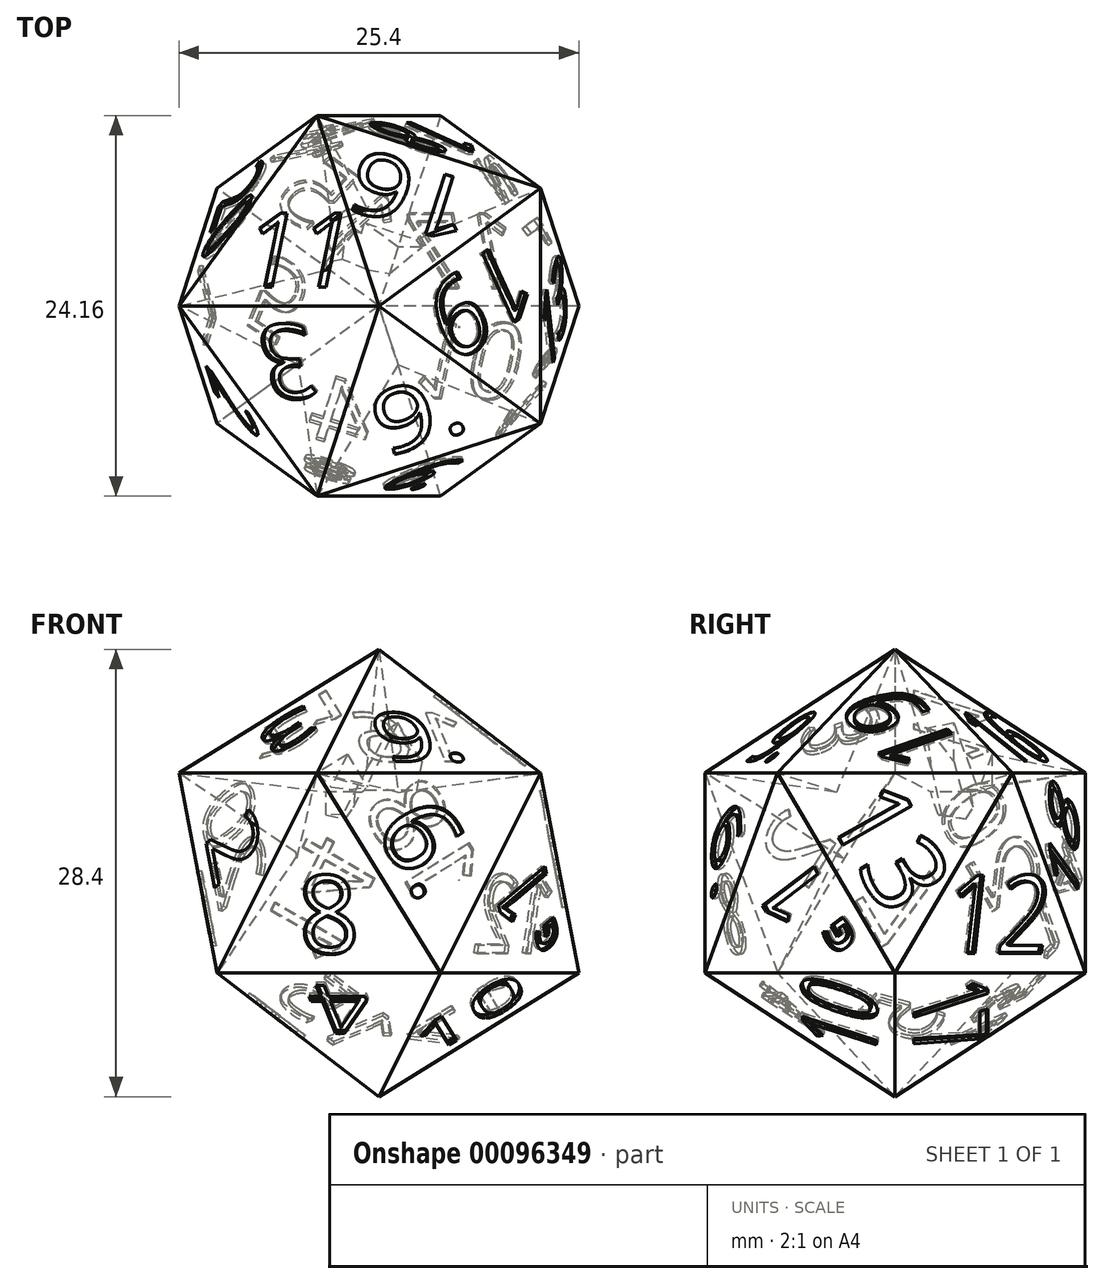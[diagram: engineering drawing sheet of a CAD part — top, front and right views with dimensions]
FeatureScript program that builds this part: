
annotation { "Feature Type Name" : "Feature", "Feature Type Description" : "" }
export const myFeature = defineFeature(function(context is Context, id is Id, definition is map)
    precondition{}
    {
        {
            var Q0;
            Q0=qCreatedBy(makeId("Top.planeOp"),FACE);
            var sketch = newSketch(context, id + "F0", { "sketchPlane" : qUnion([Q0])});
            skCircle(sketch, "E0.cCircle", {"center": v(0, 0) * mm, "radius": 12.7 * mm, "construction": true});
            skLineSegment(sketch, "E0.0", {"start": v(10.27, 7.46) * mm, "end": v(10.27, -7.46) * mm});
            skLineSegment(sketch, "E0.1", {"start": v(10.27, -7.46) * mm, "end": v(-3.92, -12.08) * mm});
            skLineSegment(sketch, "E0.2", {"start": v(-3.92, -12.08) * mm, "end": v(-12.7, 0) * mm});
            skLineSegment(sketch, "E0.3", {"start": v(-12.7, 0) * mm, "end": v(-3.92, 12.08) * mm});
            skLineSegment(sketch, "E0.4", {"start": v(-3.92, 12.08) * mm, "end": v(10.27, 7.46) * mm});
            skLineSegment(sketch, "E1", {"start": v(0, 0) * mm, "end": v(-3.92, -12.08) * mm, "construction": true});
            skSolve(sketch);
        }
        {
            var Q0;
            Q0=qCreatedBy(makeId("Right.planeOp"),FACE);
            var sketch = newSketch(context, id + "F1", { "sketchPlane" : qUnion([Q0])});
            skLineSegment(sketch, "E2", {"start": v(0, 0) * mm, "end": v(0, 7.85) * mm, "construction": true});
            skSolve(sketch);
        }
        {
            var Q0;
            Q0=sQuery(id+"F0.wireOp",VERTEX,"E0.1.start");
            var Q1;
            Q1=sQuery(id+"F0.wireOp",VERTEX,"E0.2.start");
            var Q2;
            Q2=sQuery(id+"F1.wireOp",VERTEX,"E2.end");
            cPlane(context, id + "F2", {"entities" : qUnion([Q0, Q1, Q2]), "cplaneType" : CPlaneType.THREE_POINT, "offset" : 152.4 * mm, "width" : 152.4 * mm, "height" : 152.4 * mm});
        }
        {
            var Q0;
            Q0=qCreatedBy(id+"F2.planeOp",FACE);
            var sketch = newSketch(context, id + "F3", { "sketchPlane" : qUnion([Q0])});
            skPoint(sketch, "E3.0", {"position": v(-5.19, -9.77) * mm});
            skPoint(sketch, "E4.0", {"position": v(9.27, -6.04) * mm});
            skPoint(sketch, "E5.0", {"position": v(-1.2, 4.61) * mm});
            skLineSegment(sketch, "E6", {"start": v(-5.19, -9.77) * mm, "end": v(-1.2, 4.61) * mm});
            skLineSegment(sketch, "E7", {"start": v(9.27, -6.04) * mm, "end": v(-1.2, 4.61) * mm});
            skLineSegment(sketch, "E8", {"start": v(9.27, -6.04) * mm, "end": v(-5.19, -9.77) * mm});
            skLineSegment(sketch, "E9", {"start": v(-3.19, -2.58) * mm, "end": v(9.27, -6.04) * mm, "construction": true});
            skSolve(sketch);
        }
        {
            var Q0;
            Q0=sQuery(id+"F3.wireOp",VERTEX,"E3.0");
            var Q1;
            Q1=sQuery(id+"F0.wireOp",VERTEX,"E0.2.end");
            var Q2;
            Q2=sQuery(id+"F1.wireOp",VERTEX,"E2.end");
            cPlane(context, id + "F4", {"entities" : qUnion([Q0, Q1, Q2]), "cplaneType" : CPlaneType.THREE_POINT, "offset" : 152.4 * mm, "width" : 152.4 * mm, "height" : 152.4 * mm});
        }
        {
            var Q0;
            Q0=qCreatedBy(id+"F4.planeOp",FACE);
            var sketch = newSketch(context, id + "F5", { "sketchPlane" : qUnion([Q0])});
            skPoint(sketch, "E10.0", {"position": v(-11.06, 0) * mm});
            skPoint(sketch, "E11.0", {"position": v(-0.99, -11.02) * mm});
            skPoint(sketch, "E12.0", {"position": v(3.52, 3.21) * mm});
            skLineSegment(sketch, "E13", {"start": v(-11.06, 0) * mm, "end": v(3.52, 3.21) * mm});
            skLineSegment(sketch, "E14", {"start": v(-0.99, -11.02) * mm, "end": v(-11.06, 0) * mm});
            skLineSegment(sketch, "E15", {"start": v(-0.99, -11.02) * mm, "end": v(3.52, 3.21) * mm});
            skLineSegment(sketch, "E16", {"start": v(-11.06, 0) * mm, "end": v(1.26, -3.9) * mm, "construction": true});
            skLineSegment(sketch, "E17", {"start": v(3.52, 3.21) * mm, "end": v(-6.03, -5.5) * mm, "construction": true});
            skSolve(sketch);
        }
        {
            var Q0;
            Q0=sQuery(id+"F5.wireOp",VERTEX,"E10.0");
            var Q1;
            Q1=sQuery(id+"F0.wireOp",VERTEX,"E0.3.end");
            var Q2;
            Q2=sQuery(id+"F3.wireOp",VERTEX,"E5.0");
            cPlane(context, id + "F6", {"entities" : qUnion([Q0, Q1, Q2]), "cplaneType" : CPlaneType.THREE_POINT, "offset" : 152.4 * mm, "width" : 152.4 * mm, "height" : 152.4 * mm});
        }
        {
            var Q0;
            Q0=qCreatedBy(id+"F6.planeOp",FACE);
            var sketch = newSketch(context, id + "F7", { "sketchPlane" : qUnion([Q0])});
            skPoint(sketch, "E18.0", {"position": v(-0.99, 11.02) * mm});
            skPoint(sketch, "E19.0", {"position": v(-11.06, 0) * mm});
            skPoint(sketch, "E20.0", {"position": v(3.52, -3.21) * mm});
            skLineSegment(sketch, "E21", {"start": v(-0.99, 11.02) * mm, "end": v(3.52, -3.21) * mm});
            skLineSegment(sketch, "E22", {"start": v(3.52, -3.21) * mm, "end": v(-11.06, 0) * mm});
            skLineSegment(sketch, "E23", {"start": v(-0.99, 11.02) * mm, "end": v(-11.06, 0) * mm});
            skLineSegment(sketch, "E24", {"start": v(-6.03, 5.5) * mm, "end": v(3.52, -3.21) * mm, "construction": true});
            skSolve(sketch);
        }
        {
            var Q0;
            Q0=sQuery(id+"F0.wireOp",VERTEX,"E0.4.end");
            var Q1;
            Q1=sQuery(id+"F3.wireOp",VERTEX,"E5.0");
            var Q2;
            Q2=sQuery(id+"F0.wireOp",VERTEX,"E0.3.end");
            cPlane(context, id + "F8", {"entities" : qUnion([Q0, Q1, Q2]), "cplaneType" : CPlaneType.THREE_POINT, "offset" : 152.4 * mm, "width" : 152.4 * mm, "height" : 152.4 * mm});
        }
        {
            var Q0;
            Q0=qCreatedBy(id+"F8.planeOp",FACE);
            var sketch = newSketch(context, id + "F9", { "sketchPlane" : qUnion([Q0])});
            skPoint(sketch, "E25.0", {"position": v(-5.19, 9.77) * mm});
            skPoint(sketch, "E26.0", {"position": v(9.27, 6.04) * mm});
            skPoint(sketch, "E27.0", {"position": v(-1.2, -4.61) * mm});
            skLineSegment(sketch, "E28", {"start": v(9.27, 6.04) * mm, "end": v(-1.2, -4.61) * mm});
            skLineSegment(sketch, "E29", {"start": v(-1.2, -4.61) * mm, "end": v(-5.19, 9.77) * mm});
            skLineSegment(sketch, "E30", {"start": v(-5.19, 9.77) * mm, "end": v(9.27, 6.04) * mm});
            skSolve(sketch);
        }
        {
            var Q0;
            Q0=sQuery(id+"F0.wireOp",VERTEX,"E0.4.end");
            var Q1;
            Q1=sQuery(id+"F3.wireOp",VERTEX,"E5.0");
            var Q2;
            Q2=sQuery(id+"F3.wireOp",VERTEX,"E4.0");
            cPlane(context, id + "F10", {"entities" : qUnion([Q0, Q1, Q2]), "cplaneType" : CPlaneType.THREE_POINT, "offset" : 152.4 * mm, "width" : 152.4 * mm, "height" : 152.4 * mm});
        }
        {
            var Q0;
            Q0=qCreatedBy(id+"F10.planeOp",FACE);
            var sketch = newSketch(context, id + "F11", { "sketchPlane" : qUnion([Q0])});
            skPoint(sketch, "E31.0", {"position": v(8.16, 7.46) * mm});
            skPoint(sketch, "E32.0", {"position": v(-4.76, 0) * mm});
            skPoint(sketch, "E33.0", {"position": v(8.16, -7.46) * mm});
            skLineSegment(sketch, "E34", {"start": v(8.16, 7.46) * mm, "end": v(8.16, -7.46) * mm});
            skLineSegment(sketch, "E35", {"start": v(8.16, -7.46) * mm, "end": v(-4.76, 0) * mm});
            skLineSegment(sketch, "E36", {"start": v(8.16, 7.46) * mm, "end": v(-4.76, 0) * mm});
            skSolve(sketch);
        }
        {
            var Q0;
            Q0=sQuery(id+"F5.wireOp",EDGE,"E14");
            cPlane(context, id + "F12", {"entities" : qUnion([Q0]), "cplaneType" : CPlaneType.LINE_ANGLE, "offset" : 152.4 * mm, "angle" : 100.81 * degree, "width" : 152.4 * mm, "height" : 152.4 * mm});
        }
        {
            var Q0;
            Q0=qCreatedBy(id+"F12.planeOp",FACE);
            var sketch = newSketch(context, id + "F13", { "sketchPlane" : qUnion([Q0])});
            skLineSegment(sketch, "E37", {"start": v(7.14, -2.92) * mm, "end": v(-7.66, -0.9) * mm});
            skPoint(sketch, "E38.orphan", {"position": v(-2, -14.73) * mm});
            skPoint(sketch, "E39.start.orphan", {"position": v(-0.26, -1.91) * mm});
            skPoint(sketch, "E40.start.orphan", {"position": v(2.56, -8.82) * mm});
            skLineSegment(sketch, "E41", {"start": v(7.14, -2.92) * mm, "end": v(-2, -14.72) * mm});
            skLineSegment(sketch, "E42", {"start": v(-7.66, -0.9) * mm, "end": v(-2, -14.72) * mm});
            skLineSegment(sketch, "E43", {"start": v(-0.26, -1.91) * mm, "end": v(-2, -14.72) * mm, "construction": true});
            skLineSegment(sketch, "E44", {"start": v(-4.83, -7.81) * mm, "end": v(7.14, -2.92) * mm, "construction": true});
            skSolve(sketch);
        }
        {
            var Q0;
            Q0=makeQuery(id+"F7.imprint","IMPRINT",FACE,{"disambiguationData":[TD([[makeQuery(id+"F7.imprint","IMPRINT",EDGE,{"derivedFrom":sQuery(id+"F7.wireOp",EDGE,"E21")}),-1.0]])]});
            extrude(context, id + "F14", {"entities" : qUnion([Q0]), "oppositeDirection" : true, "depth" : 2 / 76.2 * mm});
        }
        {
            var Q0;
            Q0=makeQuery(id+"F9.imprint","IMPRINT",FACE,{"disambiguationData":[TD([[makeQuery(id+"F9.imprint","IMPRINT",EDGE,{"derivedFrom":sQuery(id+"F9.wireOp",EDGE,"E28")}),-1.0]])]});
            extrude(context, id + "F15", {"entities" : qUnion([Q0]), "operationType" : NewBodyOperationType.ADD, "oppositeDirection" : true, "depth" : 2 / 76.2 * mm});
        }
        {
            var Q0;
            Q0=makeQuery(id+"F11.imprint","IMPRINT",FACE,{"disambiguationData":[TD([[makeQuery(id+"F11.imprint","IMPRINT",EDGE,{"derivedFrom":sQuery(id+"F11.wireOp",EDGE,"E34")}),-1.0]])]});
            extrude(context, id + "F16", {"entities" : qUnion([Q0]), "operationType" : NewBodyOperationType.ADD, "depth" : 16.93 * mm});
        }
        {
            var Q0;
            Q0=makeQuery(id+"F3.imprint","IMPRINT",FACE,{"disambiguationData":[TD([[makeQuery(id+"F3.imprint","IMPRINT",EDGE,{"derivedFrom":sQuery(id+"F3.wireOp",EDGE,"E6")}),-1.0]])]});
            extrude(context, id + "F17", {"entities" : qUnion([Q0]), "operationType" : NewBodyOperationType.ADD, "oppositeDirection" : true, "depth" : 2 / 76.2 * mm});
        }
        {
            var Q0;
            Q0=makeQuery(id+"F5.imprint","IMPRINT",FACE,{"disambiguationData":[TD([[makeQuery(id+"F5.imprint","IMPRINT",EDGE,{"derivedFrom":sQuery(id+"F5.wireOp",EDGE,"E13")}),-1.0]])]});
            extrude(context, id + "F18", {"entities" : qUnion([Q0]), "operationType" : NewBodyOperationType.ADD, "oppositeDirection" : true, "depth" : 18.55 * mm});
        }
        {
            var Q0;
            Q0=qSketchRegion(id+"F13",true);
            extrude(context, id + "F19", {"entities" : qUnion([Q0]), "operationType" : NewBodyOperationType.ADD, "depth" : 2 / 76.2 * mm});
        }
        {
            var Q0;
            Q0=makeQuery(id+"F19.opExtrude","CAP_EDGE",EDGE,{"disambiguationData":[OSD([sQuery(id+"F13.wireOp",EDGE,"E42")])],"isStart":true});
            cPlane(context, id + "F20", {"entities" : qUnion([Q0]), "cplaneType" : CPlaneType.LINE_ANGLE, "offset" : 152.4 * mm, "angle" : 100.81 * degree, "width" : 152.4 * mm, "height" : 152.4 * mm});
        }
        {
            var Q0;
            Q0=qCreatedBy(id+"F20.planeOp",FACE);
            var sketch = newSketch(context, id + "F21", { "sketchPlane" : qUnion([Q0])});
            skLineSegment(sketch, "E45.0", {"start": v(0.15, 2.38) * mm, "end": v(6.81, -10.98) * mm});
            skLineSegment(sketch, "E46", {"start": v(6.81, -10.98) * mm, "end": v(-8.1, -10.07) * mm});
            skLineSegment(sketch, "E47", {"start": v(-8.1, -10.07) * mm, "end": v(0.15, 2.38) * mm});
            skLineSegment(sketch, "E48", {"start": v(-8.1, -10.07) * mm, "end": v(3.48, -4.3) * mm, "construction": true});
            skSolve(sketch);
        }
        {
            var Q0;
            Q0=qSketchRegion(id+"F21",true);
            extrude(context, id + "F22", {"entities" : qUnion([Q0]), "operationType" : NewBodyOperationType.ADD, "depth" : 16.93 * mm});
        }
        {
            var Q0;
            Q0=sQuery(id+"F5.wireOp",VERTEX,"E11.0");
            var Q1;
            Q1=sQuery(id+"F3.wireOp",VERTEX,"E4.0");
            var Q2;
            Q2=makeQuery(id+"F22.opExtrude","CAP_VERTEX",VERTEX,{"disambiguationData":[OSD([sQuery(id+"F21.wireOp",EDGE,"E46"),sQuery(id+"F21.wireOp",EDGE,"E47")])],"isStart":true});
            cPlane(context, id + "F23", {"entities" : qUnion([Q0, Q1, Q2]), "cplaneType" : CPlaneType.THREE_POINT, "offset" : 152.4 * mm, "width" : 152.4 * mm, "height" : 152.4 * mm});
        }
        {
            var Q0;
            Q0=qCreatedBy(id+"F23.planeOp",FACE);
            var sketch = newSketch(context, id + "F24", { "sketchPlane" : qUnion([Q0])});
            skLineSegment(sketch, "E49.0", {"start": v(0.9, -14.83) * mm, "end": v(-7.33, -2.38) * mm});
            skLineSegment(sketch, "E50.0", {"start": v(7.57, -1.47) * mm, "end": v(-7.33, -2.38) * mm});
            skLineSegment(sketch, "E51", {"start": v(0.9, -14.83) * mm, "end": v(7.57, -1.47) * mm});
            skLineSegment(sketch, "E52", {"start": v(4.24, -8.15) * mm, "end": v(-7.33, -2.38) * mm, "construction": true});
            skSolve(sketch);
        }
        {
            var Q0;
            Q0=makeQuery(id+"F24.imprint","IMPRINT",FACE,{"disambiguationData":[TD([[makeQuery(id+"F24.imprint","IMPRINT",EDGE,{"derivedFrom":sQuery(id+"F24.wireOp",EDGE,"E49.0")}),-1.0]])]});
            extrude(context, id + "F25", {"entities" : qUnion([Q0]), "operationType" : NewBodyOperationType.ADD, "oppositeDirection" : true, "depth" : 16.93 * mm});
        }
        {
            var Q0;
            Q0=makeQuery(id+"F14.opExtrude","CAP_EDGE",EDGE,{"disambiguationData":[OSD([sQuery(id+"F7.wireOp",EDGE,"E23")])],"isStart":true});
            cPlane(context, id + "F26", {"entities" : qUnion([Q0]), "cplaneType" : CPlaneType.LINE_ANGLE, "offset" : 152.4 * mm, "angle" : 79.18 * degree, "width" : 152.4 * mm, "height" : 152.4 * mm});
        }
        {
            var Q0;
            Q0=qCreatedBy(id+"F26.planeOp",FACE);
            var sketch = newSketch(context, id + "F27", { "sketchPlane" : qUnion([Q0])});
            skLineSegment(sketch, "E53.0", {"start": v(7.66, -0.9) * mm, "end": v(-7.14, -2.92) * mm});
            skLineSegment(sketch, "E54", {"start": v(7.66, -0.9) * mm, "end": v(2, -14.72) * mm});
            skLineSegment(sketch, "E55", {"start": v(2, -14.72) * mm, "end": v(-7.14, -2.92) * mm});
            skLineSegment(sketch, "E56", {"start": v(2, -14.72) * mm, "end": v(0.26, -1.91) * mm, "construction": true});
            skLineSegment(sketch, "E57", {"start": v(4.83, -7.81) * mm, "end": v(-7.14, -2.92) * mm, "construction": true});
            skSolve(sketch);
        }
        {
            var Q0;
            Q0=qSketchRegion(id+"F27",true);
            extrude(context, id + "F28", {"entities" : qUnion([Q0]), "operationType" : NewBodyOperationType.ADD, "depth" : 6.35 * mm});
        }
        {
            var Q0;
            Q0=sQuery(id+"F7.wireOp",VERTEX,"E19.0");
            var Q1;
            Q1=makeQuery(id+"F22.boolean.opBoolean","MERGE",VERTEX,{"derivedFrom":[makeQuery(id+"F19.opExtrude","CAP_VERTEX",VERTEX,{"disambiguationData":[OSD([sQuery(id+"F13.wireOp",EDGE,"E41"),sQuery(id+"F13.wireOp",EDGE,"E42")])],"isStart":true}),makeQuery(id+"F22.opExtrude","CAP_VERTEX",VERTEX,{"disambiguationData":[OSD([sQuery(id+"F21.wireOp",EDGE,"E45.0"),sQuery(id+"F21.wireOp",EDGE,"E46")])],"isStart":true})]});
            var Q2;
            Q2=sQuery(id+"F27.wireOp",VERTEX,"E54.end");
            cPlane(context, id + "F29", {"entities" : qUnion([Q0, Q1, Q2]), "cplaneType" : CPlaneType.THREE_POINT, "offset" : 152.4 * mm, "width" : 152.4 * mm, "height" : 152.4 * mm});
        }
        {
            var Q0;
            Q0=qCreatedBy(id+"F29.planeOp",FACE);
            var sketch = newSketch(context, id + "F30", { "sketchPlane" : qUnion([Q0])});
            skLineSegment(sketch, "E58.0", {"start": v(0, 2.38) * mm, "end": v(7.46, -10.55) * mm});
            skLineSegment(sketch, "E59.0", {"start": v(-7.47, -10.55) * mm, "end": v(0, 2.38) * mm});
            skLineSegment(sketch, "E60", {"start": v(-7.47, -10.55) * mm, "end": v(7.46, -10.55) * mm});
            skSolve(sketch);
        }
        {
            var Q0;
            Q0=makeQuery(id+"F30.imprint","IMPRINT",FACE,{"disambiguationData":[TD([[makeQuery(id+"F30.imprint","IMPRINT",EDGE,{"derivedFrom":sQuery(id+"F30.wireOp",EDGE,"E58.0")}),-1.0]])]});
            extrude(context, id + "F31", {"entities" : qUnion([Q0]), "operationType" : NewBodyOperationType.ADD, "oppositeDirection" : true, "depth" : 6.35 * mm});
        }
        {
            var Q0;
            Q0=sQuery(id+"F27.wireOp",EDGE,"E54");
            cPlane(context, id + "F32", {"entities" : qUnion([Q0]), "cplaneType" : CPlaneType.LINE_ANGLE, "offset" : 152.4 * mm, "angle" : 79.19 * degree, "width" : 152.4 * mm, "height" : 152.4 * mm});
        }
        {
            var Q0;
            Q0=qCreatedBy(id+"F32.planeOp",FACE);
            var sketch = newSketch(context, id + "F33", { "sketchPlane" : qUnion([Q0])});
            skLineSegment(sketch, "E61.0", {"start": v(0.15, 2.38) * mm, "end": v(6.81, -10.98) * mm});
            skLineSegment(sketch, "E62", {"start": v(0.15, 2.38) * mm, "end": v(-8.1, -10.08) * mm});
            skLineSegment(sketch, "E63", {"start": v(-8.1, -10.08) * mm, "end": v(6.81, -10.98) * mm});
            skLineSegment(sketch, "E64", {"start": v(-8.1, -10.08) * mm, "end": v(3.48, -4.3) * mm, "construction": true});
            skLineSegment(sketch, "E65", {"start": v(0.15, 2.38) * mm, "end": v(-0.64, -10.53) * mm, "construction": true});
            skSolve(sketch);
        }
        {
            var Q0;
            Q0=qSketchRegion(id+"F33",true);
            extrude(context, id + "F34", {"entities" : qUnion([Q0]), "operationType" : NewBodyOperationType.ADD, "oppositeDirection" : true, "depth" : 6.35 * mm});
        }
        {
            var Q0;
            Q0=sQuery(id+"F33.wireOp",EDGE,"E63");
            cPlane(context, id + "F35", {"entities" : qUnion([Q0]), "cplaneType" : CPlaneType.LINE_ANGLE, "offset" : 152.4 * mm, "angle" : 52.62 * degree, "width" : 152.4 * mm, "height" : 152.4 * mm});
        }
        {
            var Q0;
            Q0=qCreatedBy(id+"F35.planeOp",FACE);
            var sketch = newSketch(context, id + "F36", { "sketchPlane" : qUnion([Q0])});
            skLineSegment(sketch, "E66.0", {"start": v(7.11, 2.3) * mm, "end": v(-7.34, -1.43) * mm});
            skLineSegment(sketch, "E67", {"start": v(7.11, 2.3) * mm, "end": v(3.12, -12.08) * mm});
            skLineSegment(sketch, "E68", {"start": v(3.12, -12.08) * mm, "end": v(-7.34, -1.43) * mm});
            skLineSegment(sketch, "E69", {"start": v(-0.11, 0.44) * mm, "end": v(3.12, -12.08) * mm, "construction": true});
            skLineSegment(sketch, "E70", {"start": v(-7.34, -1.43) * mm, "end": v(5.12, -4.89) * mm, "construction": true});
            skSolve(sketch);
        }
        {
            var Q0;
            Q0=qSketchRegion(id+"F36",true);
            extrude(context, id + "F37", {"entities" : qUnion([Q0]), "operationType" : NewBodyOperationType.ADD, "depth" : 6.35 * mm});
        }
        {
            var Q0;
            Q0=sQuery(id+"F36.wireOp",EDGE,"E67");
            cPlane(context, id + "F38", {"entities" : qUnion([Q0]), "cplaneType" : CPlaneType.LINE_ANGLE, "offset" : 152.4 * mm, "angle" : 30.6 * degree, "width" : 152.4 * mm, "height" : 152.4 * mm});
        }
        {
            var Q0;
            Q0=qCreatedBy(id+"F38.planeOp",FACE);
            var sketch = newSketch(context, id + "F39", { "sketchPlane" : qUnion([Q0])});
            skLineSegment(sketch, "E71.0", {"start": v(-4.7, -5.82) * mm, "end": v(-9.2, 8.42) * mm});
            skLineSegment(sketch, "E72", {"start": v(-4.7, -5.82) * mm, "end": v(5.37, 5.2) * mm});
            skLineSegment(sketch, "E73", {"start": v(5.37, 5.2) * mm, "end": v(-9.2, 8.42) * mm});
            skLineSegment(sketch, "E74", {"start": v(-6.96, 1.3) * mm, "end": v(5.37, 5.2) * mm, "construction": true});
            skSolve(sketch);
        }
        {
            var Q0;
            Q0=qSketchRegion(id+"F39",true);
            extrude(context, id + "F40", {"entities" : qUnion([Q0]), "operationType" : NewBodyOperationType.ADD, "oppositeDirection" : true, "depth" : 6.35 * mm});
        }
        {
            var Q0;
            Q0=sQuery(id+"F36.wireOp",VERTEX,"E66.0.start");
            var Q1;
            Q1=makeQuery(id+"F34.boolean.opBoolean","MERGE",VERTEX,{"derivedFrom":[makeQuery(id+"F28.boolean.opBoolean","MERGE",VERTEX,{"derivedFrom":[makeQuery(id+"F15.boolean.opBoolean","MERGE",VERTEX,{"derivedFrom":[makeQuery(id+"F14.opExtrude","CAP_VERTEX",VERTEX,{"disambiguationData":[OSD([sQuery(id+"F7.wireOp",EDGE,"E21"),sQuery(id+"F7.wireOp",EDGE,"E23")])],"isStart":true}),makeQuery(id+"F15.opExtrude","CAP_VERTEX",VERTEX,{"disambiguationData":[OSD([sQuery(id+"F9.wireOp",EDGE,"E29"),sQuery(id+"F9.wireOp",EDGE,"E30")])],"isStart":true})]}),makeQuery(id+"F28.opExtrude","CAP_VERTEX",VERTEX,{"disambiguationData":[OSD([sQuery(id+"F27.wireOp",EDGE,"E53.0"),sQuery(id+"F27.wireOp",EDGE,"E54")])],"isStart":true})]}),makeQuery(id+"F34.opExtrude","CAP_VERTEX",VERTEX,{"disambiguationData":[OSD([sQuery(id+"F33.wireOp",EDGE,"E61.0"),sQuery(id+"F33.wireOp",EDGE,"E62")])],"isStart":true})]});
            var Q2;
            Q2=makeQuery(id+"F16.boolean.opBoolean","MERGE",VERTEX,{"derivedFrom":[makeQuery(id+"F15.opExtrude","CAP_VERTEX",VERTEX,{"disambiguationData":[OSD([sQuery(id+"F9.wireOp",EDGE,"E28"),sQuery(id+"F9.wireOp",EDGE,"E30")])],"isStart":true}),makeQuery(id+"F16.opExtrude","CAP_VERTEX",VERTEX,{"disambiguationData":[OSD([sQuery(id+"F11.wireOp",EDGE,"E34"),sQuery(id+"F11.wireOp",EDGE,"E35")])],"isStart":true})]});
            cPlane(context, id + "F41", {"entities" : qUnion([Q0, Q1, Q2]), "cplaneType" : CPlaneType.THREE_POINT, "offset" : 152.4 * mm, "width" : 152.4 * mm, "height" : 152.4 * mm});
        }
        {
            var Q0;
            Q0=qCreatedBy(id+"F41.planeOp",FACE);
            var sketch = newSketch(context, id + "F42", { "sketchPlane" : qUnion([Q0])});
            skLineSegment(sketch, "E75.0", {"start": v(-7.33, -2.38) * mm, "end": v(7.57, -1.47) * mm});
            skLineSegment(sketch, "E76.0", {"start": v(-7.33, -2.38) * mm, "end": v(0.9, -14.83) * mm});
            skLineSegment(sketch, "E77", {"start": v(0.9, -14.83) * mm, "end": v(7.57, -1.47) * mm});
            skSolve(sketch);
        }
        {
            var Q0;
            Q0=qSketchRegion(id+"F42",true);
            extrude(context, id + "F43", {"entities" : qUnion([Q0]), "operationType" : NewBodyOperationType.ADD, "depth" : 6.35 * mm});
        }
        {
            var Q0;
            Q0=sQuery(id+"F36.wireOp",VERTEX,"E66.0.start");
            var Q1;
            Q1=makeQuery(id+"F40.opExtrude","CAP_VERTEX",VERTEX,{"disambiguationData":[OSD([sQuery(id+"F39.wireOp",EDGE,"E72"),sQuery(id+"F39.wireOp",EDGE,"E73")])],"isStart":true});
            var Q2;
            Q2=makeQuery(id+"F43.boolean.opBoolean","MERGE",VERTEX,{"derivedFrom":[makeQuery(id+"F16.boolean.opBoolean","MERGE",VERTEX,{"derivedFrom":[makeQuery(id+"F15.opExtrude","CAP_VERTEX",VERTEX,{"disambiguationData":[OSD([sQuery(id+"F9.wireOp",EDGE,"E28"),sQuery(id+"F9.wireOp",EDGE,"E30")])],"isStart":true}),makeQuery(id+"F16.opExtrude","CAP_VERTEX",VERTEX,{"disambiguationData":[OSD([sQuery(id+"F11.wireOp",EDGE,"E34"),sQuery(id+"F11.wireOp",EDGE,"E35")])],"isStart":true})]}),makeQuery(id+"F43.opExtrude","CAP_VERTEX",VERTEX,{"disambiguationData":[OSD([sQuery(id+"F42.wireOp",EDGE,"E75.0"),sQuery(id+"F42.wireOp",EDGE,"E77")])],"isStart":true})]});
            cPlane(context, id + "F44", {"entities" : qUnion([Q0, Q1, Q2]), "cplaneType" : CPlaneType.THREE_POINT, "offset" : 152.4 * mm, "width" : 152.4 * mm, "height" : 152.4 * mm});
        }
        {
            var Q0;
            Q0=qCreatedBy(id+"F44.planeOp",FACE);
            var sketch = newSketch(context, id + "F45", { "sketchPlane" : qUnion([Q0])});
            skLineSegment(sketch, "E78.0", {"start": v(5.97, -11.46) * mm, "end": v(0.32, 2.36) * mm});
            skLineSegment(sketch, "E79.0", {"start": v(5.97, -11.46) * mm, "end": v(-8.82, -9.44) * mm});
            skLineSegment(sketch, "E80", {"start": v(0.32, 2.36) * mm, "end": v(-8.82, -9.44) * mm});
            skSolve(sketch);
        }
        {
            var Q0;
            Q0=qSketchRegion(id+"F45",true);
            extrude(context, id + "F46", {"entities" : qUnion([Q0]), "operationType" : NewBodyOperationType.ADD, "oppositeDirection" : true, "depth" : 6.35 * mm});
        }
        {
            var Q0;
            Q0=makeQuery(id+"F46.boolean.opBoolean","MERGE",VERTEX,{"derivedFrom":[makeQuery(id+"F40.opExtrude","CAP_VERTEX",VERTEX,{"disambiguationData":[OSD([sQuery(id+"F39.wireOp",EDGE,"E72"),sQuery(id+"F39.wireOp",EDGE,"E73")])],"isStart":true}),makeQuery(id+"F46.opExtrude","CAP_VERTEX",VERTEX,{"disambiguationData":[OSD([sQuery(id+"F45.wireOp",EDGE,"E79.0"),sQuery(id+"F45.wireOp",EDGE,"E80")])],"isStart":true})]});
            var Q1;
            Q1=makeQuery(id+"F46.boolean.opBoolean","MERGE",VERTEX,{"derivedFrom":[makeQuery(id+"F43.boolean.opBoolean","MERGE",VERTEX,{"derivedFrom":[makeQuery(id+"F16.boolean.opBoolean","MERGE",VERTEX,{"derivedFrom":[makeQuery(id+"F15.opExtrude","CAP_VERTEX",VERTEX,{"disambiguationData":[OSD([sQuery(id+"F9.wireOp",EDGE,"E28"),sQuery(id+"F9.wireOp",EDGE,"E30")])],"isStart":true}),makeQuery(id+"F16.opExtrude","CAP_VERTEX",VERTEX,{"disambiguationData":[OSD([sQuery(id+"F11.wireOp",EDGE,"E34"),sQuery(id+"F11.wireOp",EDGE,"E35")])],"isStart":true})]}),makeQuery(id+"F43.opExtrude","CAP_VERTEX",VERTEX,{"disambiguationData":[OSD([sQuery(id+"F42.wireOp",EDGE,"E75.0"),sQuery(id+"F42.wireOp",EDGE,"E77")])],"isStart":true})]}),makeQuery(id+"F46.opExtrude","CAP_VERTEX",VERTEX,{"disambiguationData":[OSD([sQuery(id+"F45.wireOp",EDGE,"E78.0"),sQuery(id+"F45.wireOp",EDGE,"E80")])],"isStart":true})]});
            var Q2;
            Q2=makeQuery(id+"F25.boolean.opBoolean","MERGE",VERTEX,{"derivedFrom":[makeQuery(id+"F17.boolean.opBoolean","MERGE",VERTEX,{"derivedFrom":[makeQuery(id+"F16.opExtrude","CAP_VERTEX",VERTEX,{"disambiguationData":[OSD([sQuery(id+"F11.wireOp",EDGE,"E34"),sQuery(id+"F11.wireOp",EDGE,"E36")])],"isStart":true}),makeQuery(id+"F17.opExtrude","CAP_VERTEX",VERTEX,{"disambiguationData":[OSD([sQuery(id+"F3.wireOp",EDGE,"E7"),sQuery(id+"F3.wireOp",EDGE,"E8")])],"isStart":true})]}),makeQuery(id+"F25.opExtrude","CAP_VERTEX",VERTEX,{"disambiguationData":[OSD([sQuery(id+"F24.wireOp",EDGE,"E50.0"),sQuery(id+"F24.wireOp",EDGE,"E51")])],"isStart":true})]});
            cPlane(context, id + "F47", {"entities" : qUnion([Q0, Q1, Q2]), "cplaneType" : CPlaneType.THREE_POINT, "offset" : 152.4 * mm, "width" : 152.4 * mm, "height" : 152.4 * mm});
        }
        {
            var Q0;
            Q0=qCreatedBy(id+"F47.planeOp",FACE);
            var sketch = newSketch(context, id + "F48", { "sketchPlane" : qUnion([Q0])});
            skLineSegment(sketch, "E81.0", {"start": v(-7.46, -1.93) * mm, "end": v(0, -14.86) * mm});
            skLineSegment(sketch, "E82.0", {"start": v(7.46, -1.93) * mm, "end": v(-7.46, -1.93) * mm});
            skLineSegment(sketch, "E83", {"start": v(0, -14.86) * mm, "end": v(7.46, -1.93) * mm});
            skSolve(sketch);
        }
        {
            var Q0;
            Q0=qSketchRegion(id+"F48",true);
            extrude(context, id + "F49", {"entities" : qUnion([Q0]), "operationType" : NewBodyOperationType.ADD, "depth" : 6.35 * mm});
        }
        {
            var Q0;
            Q0=makeQuery(id+"F49.boolean.opBoolean","MERGE",VERTEX,{"derivedFrom":[makeQuery(id+"F46.boolean.opBoolean","MERGE",VERTEX,{"derivedFrom":[makeQuery(id+"F40.opExtrude","CAP_VERTEX",VERTEX,{"disambiguationData":[OSD([sQuery(id+"F39.wireOp",EDGE,"E72"),sQuery(id+"F39.wireOp",EDGE,"E73")])],"isStart":true}),makeQuery(id+"F46.opExtrude","CAP_VERTEX",VERTEX,{"disambiguationData":[OSD([sQuery(id+"F45.wireOp",EDGE,"E79.0"),sQuery(id+"F45.wireOp",EDGE,"E80")])],"isStart":true})]}),makeQuery(id+"F49.opExtrude","CAP_VERTEX",VERTEX,{"disambiguationData":[OSD([sQuery(id+"F48.wireOp",EDGE,"E81.0"),sQuery(id+"F48.wireOp",EDGE,"E83")])],"isStart":true})]});
            var Q1;
            Q1=makeQuery(id+"F49.boolean.opBoolean","MERGE",VERTEX,{"derivedFrom":[makeQuery(id+"F25.boolean.opBoolean","MERGE",VERTEX,{"derivedFrom":[makeQuery(id+"F17.boolean.opBoolean","MERGE",VERTEX,{"derivedFrom":[makeQuery(id+"F16.opExtrude","CAP_VERTEX",VERTEX,{"disambiguationData":[OSD([sQuery(id+"F11.wireOp",EDGE,"E34"),sQuery(id+"F11.wireOp",EDGE,"E36")])],"isStart":true}),makeQuery(id+"F17.opExtrude","CAP_VERTEX",VERTEX,{"disambiguationData":[OSD([sQuery(id+"F3.wireOp",EDGE,"E7"),sQuery(id+"F3.wireOp",EDGE,"E8")])],"isStart":true})]}),makeQuery(id+"F25.opExtrude","CAP_VERTEX",VERTEX,{"disambiguationData":[OSD([sQuery(id+"F24.wireOp",EDGE,"E50.0"),sQuery(id+"F24.wireOp",EDGE,"E51")])],"isStart":true})]}),makeQuery(id+"F49.opExtrude","CAP_VERTEX",VERTEX,{"disambiguationData":[OSD([sQuery(id+"F48.wireOp",EDGE,"E82.0"),sQuery(id+"F48.wireOp",EDGE,"E83")])],"isStart":true})]});
            var Q2;
            Q2=makeQuery(id+"F25.boolean.opBoolean","MERGE",VERTEX,{"derivedFrom":[makeQuery(id+"F22.opExtrude","CAP_VERTEX",VERTEX,{"disambiguationData":[OSD([sQuery(id+"F21.wireOp",EDGE,"E46"),sQuery(id+"F21.wireOp",EDGE,"E47")])],"isStart":true}),makeQuery(id+"F25.opExtrude","CAP_VERTEX",VERTEX,{"disambiguationData":[OSD([sQuery(id+"F24.wireOp",EDGE,"E49.0"),sQuery(id+"F24.wireOp",EDGE,"E51")])],"isStart":true})]});
            cPlane(context, id + "F50", {"entities" : qUnion([Q0, Q1, Q2]), "cplaneType" : CPlaneType.THREE_POINT, "offset" : 152.4 * mm, "width" : 152.4 * mm, "height" : 152.4 * mm});
        }
        {
            var Q0;
            Q0=qCreatedBy(id+"F50.planeOp",FACE);
            var sketch = newSketch(context, id + "F51", { "sketchPlane" : qUnion([Q0])});
            skLineSegment(sketch, "E84.0", {"start": v(-8.82, -9.44) * mm, "end": v(0.32, 2.36) * mm});
            skLineSegment(sketch, "E85.0", {"start": v(5.97, -11.46) * mm, "end": v(0.32, 2.36) * mm});
            skLineSegment(sketch, "E86", {"start": v(-8.82, -9.44) * mm, "end": v(5.97, -11.46) * mm});
            skSolve(sketch);
        }
        {
            var Q0;
            Q0=qSketchRegion(id+"F51",true);
            extrude(context, id + "F52", {"entities" : qUnion([Q0]), "operationType" : NewBodyOperationType.ADD, "depth" : 6.35 * mm});
        }
        {
            var Q0;
            Q0=makeQuery(id+"F52.boolean.opBoolean","MERGE",VERTEX,{"derivedFrom":[makeQuery(id+"F25.boolean.opBoolean","MERGE",VERTEX,{"derivedFrom":[makeQuery(id+"F22.opExtrude","CAP_VERTEX",VERTEX,{"disambiguationData":[OSD([sQuery(id+"F21.wireOp",EDGE,"E46"),sQuery(id+"F21.wireOp",EDGE,"E47")])],"isStart":true}),makeQuery(id+"F25.opExtrude","CAP_VERTEX",VERTEX,{"disambiguationData":[OSD([sQuery(id+"F24.wireOp",EDGE,"E49.0"),sQuery(id+"F24.wireOp",EDGE,"E51")])],"isStart":true})]}),makeQuery(id+"F52.opExtrude","CAP_VERTEX",VERTEX,{"disambiguationData":[OSD([sQuery(id+"F51.wireOp",EDGE,"E85.0"),sQuery(id+"F51.wireOp",EDGE,"E86")])],"isStart":true})]});
            var Q1;
            Q1=makeQuery(id+"F31.boolean.opBoolean","MERGE",VERTEX,{"derivedFrom":[makeQuery(id+"F22.boolean.opBoolean","MERGE",VERTEX,{"derivedFrom":[makeQuery(id+"F19.opExtrude","CAP_VERTEX",VERTEX,{"disambiguationData":[OSD([sQuery(id+"F13.wireOp",EDGE,"E41"),sQuery(id+"F13.wireOp",EDGE,"E42")])],"isStart":true}),makeQuery(id+"F22.opExtrude","CAP_VERTEX",VERTEX,{"disambiguationData":[OSD([sQuery(id+"F21.wireOp",EDGE,"E45.0"),sQuery(id+"F21.wireOp",EDGE,"E46")])],"isStart":true})]}),makeQuery(id+"F31.opExtrude","CAP_VERTEX",VERTEX,{"disambiguationData":[OSD([sQuery(id+"F30.wireOp",EDGE,"E58.0"),sQuery(id+"F30.wireOp",EDGE,"E60")])],"isStart":true})]});
            var Q2;
            Q2=sQuery(id+"F36.wireOp",VERTEX,"E69.end");
            cPlane(context, id + "F53", {"entities" : qUnion([Q0, Q1, Q2]), "cplaneType" : CPlaneType.THREE_POINT, "offset" : 152.4 * mm, "width" : 152.4 * mm, "height" : 152.4 * mm});
        }
        {
            var Q0;
            Q0=qCreatedBy(id+"F53.planeOp",FACE);
            var sketch = newSketch(context, id + "F54", { "sketchPlane" : qUnion([Q0])});
            skLineSegment(sketch, "E87.0", {"start": v(-7.34, 1.43) * mm, "end": v(7.11, -2.3) * mm});
            skLineSegment(sketch, "E88", {"start": v(7.11, -2.3) * mm, "end": v(3.12, 12.08) * mm});
            skLineSegment(sketch, "E89", {"start": v(3.12, 12.08) * mm, "end": v(-7.34, 1.43) * mm});
            skSolve(sketch);
        }
        {
            var Q0;
            Q0=qSketchRegion(id+"F54",true);
            extrude(context, id + "F55", {"entities" : qUnion([Q0]), "operationType" : NewBodyOperationType.ADD, "depth" : 6.35 * mm});
        }
        {
            var Q0;
            Q0=makeQuery(id+"F55.boolean.opBoolean","MERGE",VERTEX,{"derivedFrom":[makeQuery(id+"F52.boolean.opBoolean","MERGE",VERTEX,{"derivedFrom":[makeQuery(id+"F25.boolean.opBoolean","MERGE",VERTEX,{"derivedFrom":[makeQuery(id+"F22.opExtrude","CAP_VERTEX",VERTEX,{"disambiguationData":[OSD([sQuery(id+"F21.wireOp",EDGE,"E46"),sQuery(id+"F21.wireOp",EDGE,"E47")])],"isStart":true}),makeQuery(id+"F25.opExtrude","CAP_VERTEX",VERTEX,{"disambiguationData":[OSD([sQuery(id+"F24.wireOp",EDGE,"E49.0"),sQuery(id+"F24.wireOp",EDGE,"E51")])],"isStart":true})]}),makeQuery(id+"F52.opExtrude","CAP_VERTEX",VERTEX,{"disambiguationData":[OSD([sQuery(id+"F51.wireOp",EDGE,"E85.0"),sQuery(id+"F51.wireOp",EDGE,"E86")])],"isStart":true})]}),makeQuery(id+"F55.opExtrude","CAP_VERTEX",VERTEX,{"disambiguationData":[OSD([sQuery(id+"F54.wireOp",EDGE,"E87.0"),sQuery(id+"F54.wireOp",EDGE,"E88")])],"isStart":true})]});
            var Q1;
            Q1=makeQuery(id+"F52.boolean.opBoolean","MERGE",VERTEX,{"derivedFrom":[makeQuery(id+"F49.boolean.opBoolean","MERGE",VERTEX,{"derivedFrom":[makeQuery(id+"F46.boolean.opBoolean","MERGE",VERTEX,{"derivedFrom":[makeQuery(id+"F40.opExtrude","CAP_VERTEX",VERTEX,{"disambiguationData":[OSD([sQuery(id+"F39.wireOp",EDGE,"E72"),sQuery(id+"F39.wireOp",EDGE,"E73")])],"isStart":true}),makeQuery(id+"F46.opExtrude","CAP_VERTEX",VERTEX,{"disambiguationData":[OSD([sQuery(id+"F45.wireOp",EDGE,"E79.0"),sQuery(id+"F45.wireOp",EDGE,"E80")])],"isStart":true})]}),makeQuery(id+"F49.opExtrude","CAP_VERTEX",VERTEX,{"disambiguationData":[OSD([sQuery(id+"F48.wireOp",EDGE,"E81.0"),sQuery(id+"F48.wireOp",EDGE,"E83")])],"isStart":true})]}),makeQuery(id+"F52.opExtrude","CAP_VERTEX",VERTEX,{"disambiguationData":[OSD([sQuery(id+"F51.wireOp",EDGE,"E84.0"),sQuery(id+"F51.wireOp",EDGE,"E86")])],"isStart":true})]});
            var Q2;
            Q2=makeQuery(id+"F55.opExtrude","CAP_VERTEX",VERTEX,{"disambiguationData":[OSD([sQuery(id+"F54.wireOp",EDGE,"E88"),sQuery(id+"F54.wireOp",EDGE,"E89")])],"isStart":true});
            cPlane(context, id + "F56", {"entities" : qUnion([Q0, Q1, Q2]), "cplaneType" : CPlaneType.THREE_POINT, "offset" : 152.4 * mm, "width" : 152.4 * mm, "height" : 152.4 * mm});
        }
        {
            var Q0;
            Q0=qCreatedBy(id+"F56.planeOp",FACE);
            var sketch = newSketch(context, id + "F57", { "sketchPlane" : qUnion([Q0])});
            skLineSegment(sketch, "E90.0", {"start": v(-4.7, 5.82) * mm, "end": v(-9.2, -8.42) * mm});
            skPoint(sketch, "E91.0.end.orphan", {"position": v(-9.2, -8.42) * mm});
            skPoint(sketch, "E91.0.start.orphan", {"position": v(5.37, -5.2) * mm});
            skLineSegment(sketch, "E92", {"start": v(-4.7, 5.82) * mm, "end": v(5.37, -5.2) * mm});
            skLineSegment(sketch, "E93", {"start": v(5.37, -5.2) * mm, "end": v(-9.2, -8.42) * mm});
            skSolve(sketch);
        }
        {
            var Q0;
            Q0=qSketchRegion(id+"F57",true);
            extrude(context, id + "F58", {"entities" : qUnion([Q0]), "operationType" : NewBodyOperationType.ADD, "oppositeDirection" : true, "depth" : 6.35 * mm});
        }
        {
            var Q0;
            Q0=makeQuery(id+"F55.boolean.opBoolean","MERGE",VERTEX,{"derivedFrom":[makeQuery(id+"F31.boolean.opBoolean","MERGE",VERTEX,{"derivedFrom":[makeQuery(id+"F22.boolean.opBoolean","MERGE",VERTEX,{"derivedFrom":[makeQuery(id+"F19.opExtrude","CAP_VERTEX",VERTEX,{"disambiguationData":[OSD([sQuery(id+"F13.wireOp",EDGE,"E41"),sQuery(id+"F13.wireOp",EDGE,"E42")])],"isStart":true}),makeQuery(id+"F22.opExtrude","CAP_VERTEX",VERTEX,{"disambiguationData":[OSD([sQuery(id+"F21.wireOp",EDGE,"E45.0"),sQuery(id+"F21.wireOp",EDGE,"E46")])],"isStart":true})]}),makeQuery(id+"F31.opExtrude","CAP_VERTEX",VERTEX,{"disambiguationData":[OSD([sQuery(id+"F30.wireOp",EDGE,"E58.0"),sQuery(id+"F30.wireOp",EDGE,"E60")])],"isStart":true})]}),makeQuery(id+"F55.opExtrude","CAP_VERTEX",VERTEX,{"disambiguationData":[OSD([sQuery(id+"F54.wireOp",EDGE,"E87.0"),sQuery(id+"F54.wireOp",EDGE,"E89")])],"isStart":true})]});
            var Q1;
            Q1=sQuery(id+"F57.wireOp",VERTEX,"E91.0.end.orphan");
            var Q2;
            Q2=sQuery(id+"F36.wireOp",VERTEX,"E68.end");
            cPlane(context, id + "F59", {"entities" : qUnion([Q0, Q1, Q2]), "cplaneType" : CPlaneType.THREE_POINT, "offset" : 152.4 * mm, "width" : 152.4 * mm, "height" : 152.4 * mm});
        }
        {
            var Q0;
            Q0=qCreatedBy(id+"F59.planeOp",FACE);
            var sketch = newSketch(context, id + "F60", { "sketchPlane" : qUnion([Q0])});
            skLineSegment(sketch, "E94.0", {"start": v(12.48, 0) * mm, "end": v(-0.45, 7.46) * mm});
            skLineSegment(sketch, "E95", {"start": v(-0.45, 7.46) * mm, "end": v(-0.45, -7.47) * mm});
            skPoint(sketch, "E96.0.start.orphan", {"position": v(12.48, 0) * mm});
            skLineSegment(sketch, "E97", {"start": v(12.48, 0) * mm, "end": v(-0.45, -7.47) * mm});
            skSolve(sketch);
        }
        {
            var Q0;
            Q0=qSketchRegion(id+"F60",true);
            extrude(context, id + "F61", {"entities" : qUnion([Q0]), "operationType" : NewBodyOperationType.ADD, "oppositeDirection" : true, "depth" : 6.35 * mm});
        }
        {
            var Q0;
            Q0=makeQuery(id+"F28.opExtrude","CAP_FACE",FACE,{"disambiguationData":[OSD([sQuery(id+"F27.wireOp",EDGE,"E53.0"),sQuery(id+"F27.wireOp",EDGE,"E54"),sQuery(id+"F27.wireOp",EDGE,"E55")])],"isStart":true});
            var sketch = newSketch(context, id + "F62", { "sketchPlane" : qUnion([Q0])});
            skText(sketch, "E98", { "text": "20", "fontName": "OpenSans-Regular.ttf"});
            const initialGuessF62  = {"E98": [-0.0008, -0.0111, 0.61245, 0.79051, 0.00508]};
            skSetInitialGuess(sketch, initialGuessF62);
            skSolve(sketch);
        }
        {
            var Q0;
            Q0=makeQuery(id+"F14.opExtrude","CAP_FACE",FACE,{"disambiguationData":[OSD([sQuery(id+"F7.wireOp",EDGE,"E21"),sQuery(id+"F7.wireOp",EDGE,"E22"),sQuery(id+"F7.wireOp",EDGE,"E23")])],"isStart":true});
            var sketch = newSketch(context, id + "F63", { "sketchPlane" : qUnion([Q0])});
            skText(sketch, "E99", { "text": "11", "fontName": "OpenSans-Regular.ttf"});
            const initialGuessF63  = {"E99": [-0.00667, 0.00033, 0.97654, -0.21534, 0.00508]};
            skSetInitialGuess(sketch, initialGuessF63);
            skSolve(sketch);
        }
        {
            var Q0;
            Q0=makeQuery(id+"F15.opExtrude","CAP_FACE",FACE,{"disambiguationData":[OSD([sQuery(id+"F9.wireOp",EDGE,"E28"),sQuery(id+"F9.wireOp",EDGE,"E29"),sQuery(id+"F9.wireOp",EDGE,"E30")])],"isStart":true});
            var sketch = newSketch(context, id + "F64", { "sketchPlane" : qUnion([Q0])});
            skText(sketch, "E100", { "text": "16", "fontName": "OpenSans-Regular.ttf"});
            const initialGuessF64  = {"E100": [0.00546, 0.00571, -0.96824, 0.25, 0.00508]};
            skSetInitialGuess(sketch, initialGuessF64);
            skSolve(sketch);
        }
        {
            var Q0;
            Q0=makeQuery(id+"F43.opExtrude","CAP_FACE",FACE,{"disambiguationData":[OSD([sQuery(id+"F42.wireOp",EDGE,"E75.0"),sQuery(id+"F42.wireOp",EDGE,"E76.0"),sQuery(id+"F42.wireOp",EDGE,"E77")])],"isStart":true});
            var sketch = newSketch(context, id + "F65", { "sketchPlane" : qUnion([Q0])});
            skText(sketch, "E101", { "text": "18", "fontName": "OpenSans-Regular.ttf"});
            const initialGuessF65  = {"E101": [3e-05, -0.01112, 0.55168, 0.83405, 0.00508]};
            skSetInitialGuess(sketch, initialGuessF65);
            skSolve(sketch);
        }
        {
            var Q0;
            Q0=makeQuery(id+"F34.opExtrude","CAP_FACE",FACE,{"disambiguationData":[OSD([sQuery(id+"F33.wireOp",EDGE,"E61.0"),sQuery(id+"F33.wireOp",EDGE,"E62"),sQuery(id+"F33.wireOp",EDGE,"E63")])],"isStart":true});
            var sketch = newSketch(context, id + "F66", { "sketchPlane" : qUnion([Q0])});
            skText(sketch, "E102", { "text": "14\n", "fontName": "OpenSans-Regular.ttf"});
            const initialGuessF66  = {"E102": [0.00411, -0.00842, -0.44648, 0.8948, 0.00508]};
            skSetInitialGuess(sketch, initialGuessF66);
            skSolve(sketch);
        }
        {
            var Q0;
            Q0=makeQuery(id+"F18.opExtrude","CAP_FACE",FACE,{"disambiguationData":[OSD([sQuery(id+"F5.wireOp",EDGE,"E13"),sQuery(id+"F5.wireOp",EDGE,"E14"),sQuery(id+"F5.wireOp",EDGE,"E15")])],"isStart":true});
            var sketch = newSketch(context, id + "F67", { "sketchPlane" : qUnion([Q0])});
            skText(sketch, "E103", { "text": "3\n", "fontName": "OpenSans-Regular.ttf"});
            const initialGuessF67  = {"E103": [-0.00173, 0.00076, -0.97654, -0.21534, 0.00508]};
            skSetInitialGuess(sketch, initialGuessF67);
            skSolve(sketch);
        }
        {
            var Q0;
            Q0=makeQuery(id+"F16.opExtrude","CAP_FACE",FACE,{"disambiguationData":[OSD([sQuery(id+"F11.wireOp",EDGE,"E34"),sQuery(id+"F11.wireOp",EDGE,"E35"),sQuery(id+"F11.wireOp",EDGE,"E36")])],"isStart":true});
            var sketch = newSketch(context, id + "F68", { "sketchPlane" : qUnion([Q0])});
            skText(sketch, "E104", { "text": "19", "fontName": "OpenSans-Regular.ttf"});
            const initialGuessF68  = {"E104": [0.00566, 0.00455, -0.86602, -0.5, 0.00508]};
            skSetInitialGuess(sketch, initialGuessF68);
            skSolve(sketch);
        }
        {
            var Q0;
            Q0=makeQuery(id+"F46.opExtrude","CAP_FACE",FACE,{"disambiguationData":[OSD([sQuery(id+"F45.wireOp",EDGE,"E78.0"),sQuery(id+"F45.wireOp",EDGE,"E79.0"),sQuery(id+"F45.wireOp",EDGE,"E80")])],"isStart":true});
            var sketch = newSketch(context, id + "F69", { "sketchPlane" : qUnion([Q0])});
            skText(sketch, "E105", { "text": "12", "fontName": "OpenSans-Regular.ttf"});
            const initialGuessF69  = {"E105": [-0.00506, -0.00867, 0.99084, -0.13504, 0.00508]};
            skSetInitialGuess(sketch, initialGuessF69);
            skSolve(sketch);
        }
        {
            var Q0;
            Q0=makeQuery(id+"F37.opExtrude","CAP_FACE",FACE,{"disambiguationData":[OSD([sQuery(id+"F36.wireOp",EDGE,"E66.0"),sQuery(id+"F36.wireOp",EDGE,"E67"),sQuery(id+"F36.wireOp",EDGE,"E68")])],"isStart":true});
            var sketch = newSketch(context, id + "F70", { "sketchPlane" : qUnion([Q0])});
            skSolve(sketch);
        }
        {
            var Q0;
            Q0=makeQuery(id+"F70.imprint","IMPRINT",FACE,{"disambiguationData":[TD([[makeQuery(id+"F70.imprint","IMPRINT",EDGE,{"derivedFrom":makeQuery(id+"F37.opExtrude","CAP_EDGE",EDGE,{"disambiguationData":[OSD([sQuery(id+"F36.wireOp",EDGE,"E68")])],"isStart":true})}),1.0]])]});
            var sketch = newSketch(context, id + "F71", { "sketchPlane" : qUnion([Q0])});
            skText(sketch, "E106", { "text": "15", "fontName": "OpenSans-Regular.ttf"});
            const initialGuessF71  = {"E106": [0.00148, 0.0086, -0.70055, -0.7136, 0.00508]};
            skSetInitialGuess(sketch, initialGuessF71);
            skSolve(sketch);
        }
        {
            var Q0;
            Q0=makeQuery(id+"F31.opExtrude","CAP_FACE",FACE,{"disambiguationData":[OSD([sQuery(id+"F30.wireOp",EDGE,"E58.0"),sQuery(id+"F30.wireOp",EDGE,"E59.0"),sQuery(id+"F30.wireOp",EDGE,"E60")])],"isStart":true});
            var sketch = newSketch(context, id + "F72", { "sketchPlane" : qUnion([Q0])});
            skText(sketch, "E107", { "text": "7", "fontName": "OpenSans-Regular.ttf"});
            const initialGuessF72  = {"E107": [-0.00171, -0.00313, -0.50007, -0.86599, 0.00508]};
            skSetInitialGuess(sketch, initialGuessF72);
            skSolve(sketch);
        }
        {
            var Q0;
            Q0=makeQuery(id+"F61.opExtrude","CAP_FACE",FACE,{"disambiguationData":[OSD([sQuery(id+"F60.wireOp",EDGE,"E94.0"),sQuery(id+"F60.wireOp",EDGE,"E95"),sQuery(id+"F60.wireOp",EDGE,"E97")])],"isStart":true});
            var sketch = newSketch(context, id + "F73", { "sketchPlane" : qUnion([Q0])});
            skText(sketch, "E108", { "text": "5", "fontName": "OpenSans-Regular.ttf"});
            const initialGuessF73  = {"E108": [0.0038, -0.00354, 0.86603, 0.5, 0.00508]};
            skSetInitialGuess(sketch, initialGuessF73);
            skSolve(sketch);
        }
        {
            var Q0;
            Q0=makeQuery(id+"F55.opExtrude","CAP_FACE",FACE,{"disambiguationData":[OSD([sQuery(id+"F54.wireOp",EDGE,"E87.0"),sQuery(id+"F54.wireOp",EDGE,"E88"),sQuery(id+"F54.wireOp",EDGE,"E89")])],"isStart":true});
            var sketch = newSketch(context, id + "F74", { "sketchPlane" : qUnion([Q0])});
            skText(sketch, "E109", { "text": "4", "fontName": "OpenSans-Regular.ttf"});
            const initialGuessF74  = {"E109": [0.00209, -0.0003, -0.96826, -0.24996, 0.00508]};
            skSetInitialGuess(sketch, initialGuessF74);
            skSolve(sketch);
        }
        {
            var Q0;
            Q0=makeQuery(id+"F22.opExtrude","CAP_FACE",FACE,{"disambiguationData":[OSD([sQuery(id+"F21.wireOp",EDGE,"E45.0"),sQuery(id+"F21.wireOp",EDGE,"E46"),sQuery(id+"F21.wireOp",EDGE,"E47")])],"isStart":true});
            var sketch = newSketch(context, id + "F75", { "sketchPlane" : qUnion([Q0])});
            skText(sketch, "E110", { "text": "8", "fontName": "OpenSans-Regular.ttf"});
            const initialGuessF75  = {"E110": [-0.00127, -0.00937, 0.99815, 0.0608, 0.00508]};
            skSetInitialGuess(sketch, initialGuessF75);
            skSolve(sketch);
        }
        {
            var Q0;
            Q0=makeQuery(id+"F19.opExtrude","CAP_FACE",FACE,{"disambiguationData":[OSD([sQuery(id+"F13.wireOp",EDGE,"E37"),sQuery(id+"F13.wireOp",EDGE,"E41"),sQuery(id+"F13.wireOp",EDGE,"E42")])],"isStart":true});
            var sketch = newSketch(context, id + "F76", { "sketchPlane" : qUnion([Q0])});
            skText(sketch, "E111", { "text": "2", "fontName": "OpenSans-Regular.ttf"});
            const initialGuessF76  = {"E111": [-0.00268, -0.0066, 0.6124, -0.79055, 0.00508]};
            skSetInitialGuess(sketch, initialGuessF76);
            skSolve(sketch);
        }
        {
            var Q0;
            Q0=makeQuery(id+"F25.opExtrude","CAP_FACE",FACE,{"disambiguationData":[OSD([sQuery(id+"F24.wireOp",EDGE,"E49.0"),sQuery(id+"F24.wireOp",EDGE,"E50.0"),sQuery(id+"F24.wireOp",EDGE,"E51")])],"isStart":true});
            var sketch = newSketch(context, id + "F77", { "sketchPlane" : qUnion([Q0])});
            skText(sketch, "E112", { "text": "6.", "fontName": "OpenSans-Regular.ttf"});
            const initialGuessF77  = {"E112": [-0.00364, -0.00566, 0.55174, -0.83402, 0.00508]};
            skSetInitialGuess(sketch, initialGuessF77);
            skSolve(sketch);
        }
        {
            var Q0;
            Q0=makeQuery(id+"F17.opExtrude","CAP_FACE",FACE,{"disambiguationData":[OSD([sQuery(id+"F3.wireOp",EDGE,"E6"),sQuery(id+"F3.wireOp",EDGE,"E7"),sQuery(id+"F3.wireOp",EDGE,"E8")])],"isStart":true});
            var sketch = newSketch(context, id + "F78", { "sketchPlane" : qUnion([Q0])});
            skText(sketch, "E113", { "text": "9.", "fontName": "OpenSans-Regular.ttf"});
            const initialGuessF78  = {"E113": [-0.00088, -0.00735, 0.96824, 0.25, 0.00508]};
            skSetInitialGuess(sketch, initialGuessF78);
            skSolve(sketch);
        }
        {
            var Q0;
            Q0=makeQuery(id+"F52.opExtrude","CAP_FACE",FACE,{"disambiguationData":[OSD([sQuery(id+"F51.wireOp",EDGE,"E84.0"),sQuery(id+"F51.wireOp",EDGE,"E85.0"),sQuery(id+"F51.wireOp",EDGE,"E86")])],"isStart":true});
            var sketch = newSketch(context, id + "F79", { "sketchPlane" : qUnion([Q0])});
            skText(sketch, "E114", { "text": "1", "fontName": "OpenSans-Regular.ttf"});
            const initialGuessF79  = {"E114": [0.004, -0.0053, -0.61228, 0.79064, 0.00508]};
            skSetInitialGuess(sketch, initialGuessF79);
            skSolve(sketch);
        }
        {
            var Q0;
            Q0=makeQuery(id+"F49.opExtrude","CAP_FACE",FACE,{"disambiguationData":[OSD([sQuery(id+"F48.wireOp",EDGE,"E81.0"),sQuery(id+"F48.wireOp",EDGE,"E82.0"),sQuery(id+"F48.wireOp",EDGE,"E83")])],"isStart":true});
            var sketch = newSketch(context, id + "F80", { "sketchPlane" : qUnion([Q0])});
            skText(sketch, "E115", { "text": "13", "fontName": "OpenSans-Regular.ttf"});
            const initialGuessF80  = {"E115": [-0.00455, -0.00444, 0.49995, -0.86605, 0.00508]};
            skSetInitialGuess(sketch, initialGuessF80);
            skSolve(sketch);
        }
        {
            var Q0;
            Q0=makeQuery(id+"F58.opExtrude","CAP_FACE",FACE,{"disambiguationData":[OSD([sQuery(id+"F57.wireOp",EDGE,"E90.0"),sQuery(id+"F57.wireOp",EDGE,"E92"),sQuery(id+"F57.wireOp",EDGE,"E93")])],"isStart":true});
            var sketch = newSketch(context, id + "F81", { "sketchPlane" : qUnion([Q0])});
            skText(sketch, "E116", { "text": "10", "fontName": "OpenSans-Regular.ttf"});
            const initialGuessF81  = {"E116": [-0.00596, -0.0064, 0.97653, 0.21539, 0.00508]};
            skSetInitialGuess(sketch, initialGuessF81);
            skSolve(sketch);
        }
        {
            var Q0;
            Q0=makeQuery(id+"F40.opExtrude","CAP_FACE",FACE,{"disambiguationData":[OSD([sQuery(id+"F39.wireOp",EDGE,"E71.0"),sQuery(id+"F39.wireOp",EDGE,"E72"),sQuery(id+"F39.wireOp",EDGE,"E73")])],"isStart":true});
            var sketch = newSketch(context, id + "F82", { "sketchPlane" : qUnion([Q0])});
            skText(sketch, "E117", { "text": "17", "fontName": "OpenSans-Regular.ttf"});
            const initialGuessF82  = {"E117": [0.00157, 0.00474, -0.97654, 0.21531, 0.00508]};
            skSetInitialGuess(sketch, initialGuessF82);
            skSolve(sketch);
        }
        {
            var Q0;
            Q0=makeQuery(id+"F81.imprint","IMPRINT",FACE,{"disambiguationData":[TD([[makeQuery(id+"F81.imprint","IMPRINT",EDGE,{"derivedFrom":sQuery(id+"F81.wireOp",EDGE,"E116.sketch_text.stroke-9")}),-1.0]])]});
            var Q1;
            Q1=makeQuery(id+"F81.imprint","IMPRINT",FACE,{"disambiguationData":[TD([[makeQuery(id+"F81.imprint","IMPRINT",EDGE,{"derivedFrom":sQuery(id+"F81.wireOp",EDGE,"E116.sketch_text.stroke-0")}),-1.0]])]});
            extrude(context, id + "F83", {"entities" : qUnion([Q0, Q1]), "operationType" : NewBodyOperationType.REMOVE, "oppositeDirection" : true, "depth" : 0.25 * mm});
        }
        {
            var Q0;
            Q0=makeQuery(id+"F82.imprint","IMPRINT",FACE,{"disambiguationData":[TD([[makeQuery(id+"F82.imprint","IMPRINT",EDGE,{"derivedFrom":sQuery(id+"F82.wireOp",EDGE,"E117.sketch_text.stroke-0")}),-1.0]])]});
            var Q1;
            Q1=makeQuery(id+"F82.imprint","IMPRINT",FACE,{"disambiguationData":[TD([[makeQuery(id+"F82.imprint","IMPRINT",EDGE,{"derivedFrom":sQuery(id+"F82.wireOp",EDGE,"E117.sketch_text.stroke-9")}),-1.0]])]});
            extrude(context, id + "F84", {"entities" : qUnion([Q0, Q1]), "operationType" : NewBodyOperationType.REMOVE, "oppositeDirection" : true, "depth" : 0.25 * mm});
        }
        {
            var Q0;
            Q0=makeQuery(id+"F71.imprint","IMPRINT",FACE,{"disambiguationData":[TD([[makeQuery(id+"F71.imprint","IMPRINT",EDGE,{"derivedFrom":sQuery(id+"F71.wireOp",EDGE,"E106.sketch_text.stroke-0")}),-1.0]])]});
            var Q1;
            Q1=makeQuery(id+"F71.imprint","IMPRINT",FACE,{"disambiguationData":[TD([[makeQuery(id+"F71.imprint","IMPRINT",EDGE,{"derivedFrom":sQuery(id+"F71.wireOp",EDGE,"E106.sketch_text.stroke-9")}),-1.0]])]});
            extrude(context, id + "F85", {"entities" : qUnion([Q0, Q1]), "operationType" : NewBodyOperationType.REMOVE, "oppositeDirection" : true, "depth" : 0.25 * mm});
        }
        {
            var Q0;
            Q0=makeQuery(id+"F73.imprint","IMPRINT",FACE,{"disambiguationData":[TD([[makeQuery(id+"F73.imprint","IMPRINT",EDGE,{"derivedFrom":sQuery(id+"F73.wireOp",EDGE,"E108.sketch_text.stroke-0")}),-1.0]])]});
            extrude(context, id + "F86", {"entities" : qUnion([Q0]), "operationType" : NewBodyOperationType.REMOVE, "oppositeDirection" : true, "depth" : 0.25 * mm});
        }
        {
            var Q0;
            Q0=makeQuery(id+"F74.imprint","IMPRINT",FACE,{"disambiguationData":[TD([[makeQuery(id+"F74.imprint","IMPRINT",EDGE,{"derivedFrom":sQuery(id+"F74.wireOp",EDGE,"E109.sketch_text.stroke-0")}),-1.0]])]});
            extrude(context, id + "F87", {"entities" : qUnion([Q0]), "operationType" : NewBodyOperationType.REMOVE, "oppositeDirection" : true, "depth" : 0.25 * mm});
        }
        {
            var Q0;
            Q0=makeQuery(id+"F75.imprint","IMPRINT",FACE,{"disambiguationData":[TD([[makeQuery(id+"F75.imprint","IMPRINT",EDGE,{"derivedFrom":sQuery(id+"F75.wireOp",EDGE,"E110.sketch_text.stroke-0")}),-1.0]])]});
            extrude(context, id + "F88", {"entities" : qUnion([Q0]), "operationType" : NewBodyOperationType.REMOVE, "oppositeDirection" : true, "depth" : 0.25 * mm});
        }
        {
            var Q0;
            Q0=makeQuery(id+"F77.imprint","IMPRINT",FACE,{"disambiguationData":[TD([[makeQuery(id+"F77.imprint","IMPRINT",EDGE,{"derivedFrom":sQuery(id+"F77.wireOp",EDGE,"E112.sketch_text.stroke-0")}),-1.0]])]});
            var Q1;
            Q1=makeQuery(id+"F77.imprint","IMPRINT",FACE,{"disambiguationData":[TD([[makeQuery(id+"F77.imprint","IMPRINT",EDGE,{"derivedFrom":sQuery(id+"F77.wireOp",EDGE,"E112.sketch_text.stroke-25")}),-1.0]])]});
            extrude(context, id + "F89", {"entities" : qUnion([Q0, Q1]), "operationType" : NewBodyOperationType.REMOVE, "oppositeDirection" : true, "depth" : 0.25 * mm});
        }
        {
            var Q0;
            Q0=makeQuery(id+"F79.imprint","IMPRINT",FACE,{"disambiguationData":[TD([[makeQuery(id+"F79.imprint","IMPRINT",EDGE,{"derivedFrom":sQuery(id+"F79.wireOp",EDGE,"E114.sketch_text.stroke-0")}),-1.0]])]});
            extrude(context, id + "F90", {"entities" : qUnion([Q0]), "operationType" : NewBodyOperationType.REMOVE, "oppositeDirection" : true, "depth" : 0.25 * mm});
        }
        {
            var Q0;
            Q0=makeQuery(id+"F69.imprint","IMPRINT",FACE,{"disambiguationData":[TD([[makeQuery(id+"F69.imprint","IMPRINT",EDGE,{"derivedFrom":sQuery(id+"F69.wireOp",EDGE,"E105.sketch_text.stroke-0")}),-1.0]])]});
            var Q1;
            Q1=makeQuery(id+"F69.imprint","IMPRINT",FACE,{"disambiguationData":[TD([[makeQuery(id+"F69.imprint","IMPRINT",EDGE,{"derivedFrom":sQuery(id+"F69.wireOp",EDGE,"E105.sketch_text.stroke-9")}),-1.0]])]});
            extrude(context, id + "F91", {"entities" : qUnion([Q0, Q1]), "operationType" : NewBodyOperationType.REMOVE, "oppositeDirection" : true, "depth" : 0.28 * mm});
        }
        {
            var Q0;
            Q0=makeQuery(id+"F80.imprint","IMPRINT",FACE,{"disambiguationData":[TD([[makeQuery(id+"F80.imprint","IMPRINT",EDGE,{"derivedFrom":sQuery(id+"F80.wireOp",EDGE,"E115.sketch_text.stroke-9")}),-1.0]])]});
            var Q1;
            Q1=makeQuery(id+"F80.imprint","IMPRINT",FACE,{"disambiguationData":[TD([[makeQuery(id+"F80.imprint","IMPRINT",EDGE,{"derivedFrom":sQuery(id+"F80.wireOp",EDGE,"E115.sketch_text.stroke-0")}),-1.0]])]});
            extrude(context, id + "F92", {"entities" : qUnion([Q0, Q1]), "operationType" : NewBodyOperationType.REMOVE, "oppositeDirection" : true, "depth" : 0.25 * mm});
        }
        {
            var Q0;
            Q0=makeQuery(id+"F65.imprint","IMPRINT",FACE,{"disambiguationData":[TD([[makeQuery(id+"F65.imprint","IMPRINT",EDGE,{"derivedFrom":sQuery(id+"F65.wireOp",EDGE,"E101.sketch_text.stroke-9")}),-1.0]])]});
            var Q1;
            Q1=makeQuery(id+"F65.imprint","IMPRINT",FACE,{"disambiguationData":[TD([[makeQuery(id+"F65.imprint","IMPRINT",EDGE,{"derivedFrom":sQuery(id+"F65.wireOp",EDGE,"E101.sketch_text.stroke-0")}),-1.0]])]});
            extrude(context, id + "F93", {"entities" : qUnion([Q0, Q1]), "operationType" : NewBodyOperationType.REMOVE, "oppositeDirection" : true, "depth" : 0.25 * mm});
        }
        {
            var Q0;
            Q0=makeQuery(id+"F66.imprint","IMPRINT",FACE,{"disambiguationData":[TD([[makeQuery(id+"F66.imprint","IMPRINT",EDGE,{"derivedFrom":sQuery(id+"F66.wireOp",EDGE,"E102.sketch_text.stroke-0")}),-1.0]])]});
            var Q1;
            Q1=makeQuery(id+"F66.imprint","IMPRINT",FACE,{"disambiguationData":[TD([[makeQuery(id+"F66.imprint","IMPRINT",EDGE,{"derivedFrom":sQuery(id+"F66.wireOp",EDGE,"E102.sketch_text.stroke-9")}),-1.0]])]});
            extrude(context, id + "F94", {"entities" : qUnion([Q0, Q1]), "operationType" : NewBodyOperationType.REMOVE, "oppositeDirection" : true, "depth" : 0.25 * mm});
        }
        {
            var Q0;
            Q0=makeQuery(id+"F62.imprint","IMPRINT",FACE,{"disambiguationData":[TD([[makeQuery(id+"F62.imprint","IMPRINT",EDGE,{"derivedFrom":sQuery(id+"F62.wireOp",EDGE,"E98.sketch_text.stroke-0")}),-1.0]])]});
            var Q1;
            Q1=makeQuery(id+"F62.imprint","IMPRINT",FACE,{"disambiguationData":[TD([[makeQuery(id+"F62.imprint","IMPRINT",EDGE,{"derivedFrom":sQuery(id+"F62.wireOp",EDGE,"E98.sketch_text.stroke-20")}),-1.0]])]});
            extrude(context, id + "F95", {"entities" : qUnion([Q0, Q1]), "operationType" : NewBodyOperationType.REMOVE, "oppositeDirection" : true, "depth" : 0.25 * mm});
        }
        {
            var Q0;
            Q0=makeQuery(id+"F64.imprint","IMPRINT",FACE,{"disambiguationData":[TD([[makeQuery(id+"F64.imprint","IMPRINT",EDGE,{"derivedFrom":sQuery(id+"F64.wireOp",EDGE,"E100.sketch_text.stroke-9")}),-1.0]])]});
            var Q1;
            Q1=makeQuery(id+"F64.imprint","IMPRINT",FACE,{"disambiguationData":[TD([[makeQuery(id+"F64.imprint","IMPRINT",EDGE,{"derivedFrom":sQuery(id+"F64.wireOp",EDGE,"E100.sketch_text.stroke-0")}),-1.0]])]});
            extrude(context, id + "F96", {"entities" : qUnion([Q0, Q1]), "operationType" : NewBodyOperationType.REMOVE, "oppositeDirection" : true, "depth" : 0.25 * mm});
        }
        {
            var Q0;
            Q0=makeQuery(id+"F63.imprint","IMPRINT",FACE,{"disambiguationData":[TD([[makeQuery(id+"F63.imprint","IMPRINT",EDGE,{"derivedFrom":sQuery(id+"F63.wireOp",EDGE,"E99.sketch_text.stroke-0")}),-1.0]])]});
            var Q1;
            Q1=makeQuery(id+"F63.imprint","IMPRINT",FACE,{"disambiguationData":[TD([[makeQuery(id+"F63.imprint","IMPRINT",EDGE,{"derivedFrom":sQuery(id+"F63.wireOp",EDGE,"E99.sketch_text.stroke-9")}),-1.0]])]});
            extrude(context, id + "F97", {"entities" : qUnion([Q0, Q1]), "operationType" : NewBodyOperationType.REMOVE, "oppositeDirection" : true, "depth" : 0.25 * mm});
        }
        {
            var Q0;
            Q0=makeQuery(id+"F68.imprint","IMPRINT",FACE,{"disambiguationData":[TD([[makeQuery(id+"F68.imprint","IMPRINT",EDGE,{"derivedFrom":sQuery(id+"F68.wireOp",EDGE,"E104.sketch_text.stroke-9")}),-1.0]])]});
            var Q1;
            Q1=makeQuery(id+"F68.imprint","IMPRINT",FACE,{"disambiguationData":[TD([[makeQuery(id+"F68.imprint","IMPRINT",EDGE,{"derivedFrom":sQuery(id+"F68.wireOp",EDGE,"E104.sketch_text.stroke-0")}),-1.0]])]});
            extrude(context, id + "F98", {"entities" : qUnion([Q0, Q1]), "operationType" : NewBodyOperationType.REMOVE, "oppositeDirection" : true, "depth" : 0.25 * mm});
        }
        {
            var Q0;
            Q0=makeQuery(id+"F78.imprint","IMPRINT",FACE,{"disambiguationData":[TD([[makeQuery(id+"F78.imprint","IMPRINT",EDGE,{"derivedFrom":sQuery(id+"F78.wireOp",EDGE,"E113.sketch_text.stroke-0")}),-1.0]])]});
            var Q1;
            Q1=makeQuery(id+"F78.imprint","IMPRINT",FACE,{"disambiguationData":[TD([[makeQuery(id+"F78.imprint","IMPRINT",EDGE,{"derivedFrom":sQuery(id+"F78.wireOp",EDGE,"E113.sketch_text.stroke-26")}),-1.0]])]});
            extrude(context, id + "F99", {"entities" : qUnion([Q0, Q1]), "operationType" : NewBodyOperationType.REMOVE, "oppositeDirection" : true, "depth" : 0.25 * mm});
        }
        {
            var Q0;
            Q0=makeQuery(id+"F72.imprint","IMPRINT",FACE,{"disambiguationData":[TD([[makeQuery(id+"F72.imprint","IMPRINT",EDGE,{"derivedFrom":sQuery(id+"F72.wireOp",EDGE,"E107.sketch_text.stroke-0")}),-1.0]])]});
            extrude(context, id + "F100", {"entities" : qUnion([Q0]), "operationType" : NewBodyOperationType.REMOVE, "oppositeDirection" : true, "depth" : 0.25 * mm});
        }
        {
            var Q0;
            Q0=makeQuery(id+"F76.imprint","IMPRINT",FACE,{"disambiguationData":[TD([[makeQuery(id+"F76.imprint","IMPRINT",EDGE,{"derivedFrom":sQuery(id+"F76.wireOp",EDGE,"E111.sketch_text.stroke-0")}),-1.0]])]});
            extrude(context, id + "F101", {"entities" : qUnion([Q0]), "operationType" : NewBodyOperationType.REMOVE, "oppositeDirection" : true, "depth" : 0.25 * mm});
        }
        {
            var Q0;
            Q0=makeQuery(id+"F67.imprint","IMPRINT",FACE,{"disambiguationData":[TD([[makeQuery(id+"F67.imprint","IMPRINT",EDGE,{"derivedFrom":sQuery(id+"F67.wireOp",EDGE,"E103.sketch_text.stroke-0")}),-1.0]])]});
            extrude(context, id + "F102", {"entities" : qUnion([Q0]), "operationType" : NewBodyOperationType.REMOVE, "oppositeDirection" : true, "depth" : 0.25 * mm});
        }
        {
            var Q0;
            Q0=makeQuery(id+"F52.opExtrude","CAP_FACE",FACE,{"disambiguationData":[OSD([sQuery(id+"F51.wireOp",EDGE,"E84.0"),sQuery(id+"F51.wireOp",EDGE,"E85.0"),sQuery(id+"F51.wireOp",EDGE,"E86")])],"isStart":true});
            var sketch = newSketch(context, id + "F103", { "sketchPlane" : qUnion([Q0])});
            skText(sketch, "E118", { "text": "G", "fontName": "OpenSans-Bold.ttf"});
            const initialGuessF103  = {"E118": [0.00593, -0.0078, -0.61228, 0.79064, 0.00211]};
            skSetInitialGuess(sketch, initialGuessF103);
            skSolve(sketch);
        }
        {
            var Q0;
            Q0=makeQuery(id+"F103.imprint","IMPRINT",FACE,{"disambiguationData":[TD([[makeQuery(id+"F103.imprint","IMPRINT",EDGE,{"derivedFrom":sQuery(id+"F103.wireOp",EDGE,"E118.sketch_text.stroke-0")}),-1.0]])]});
            extrude(context, id + "F104", {"entities" : qUnion([Q0]), "operationType" : NewBodyOperationType.REMOVE, "oppositeDirection" : true, "depth" : 0.25 * mm});
        }
    });
